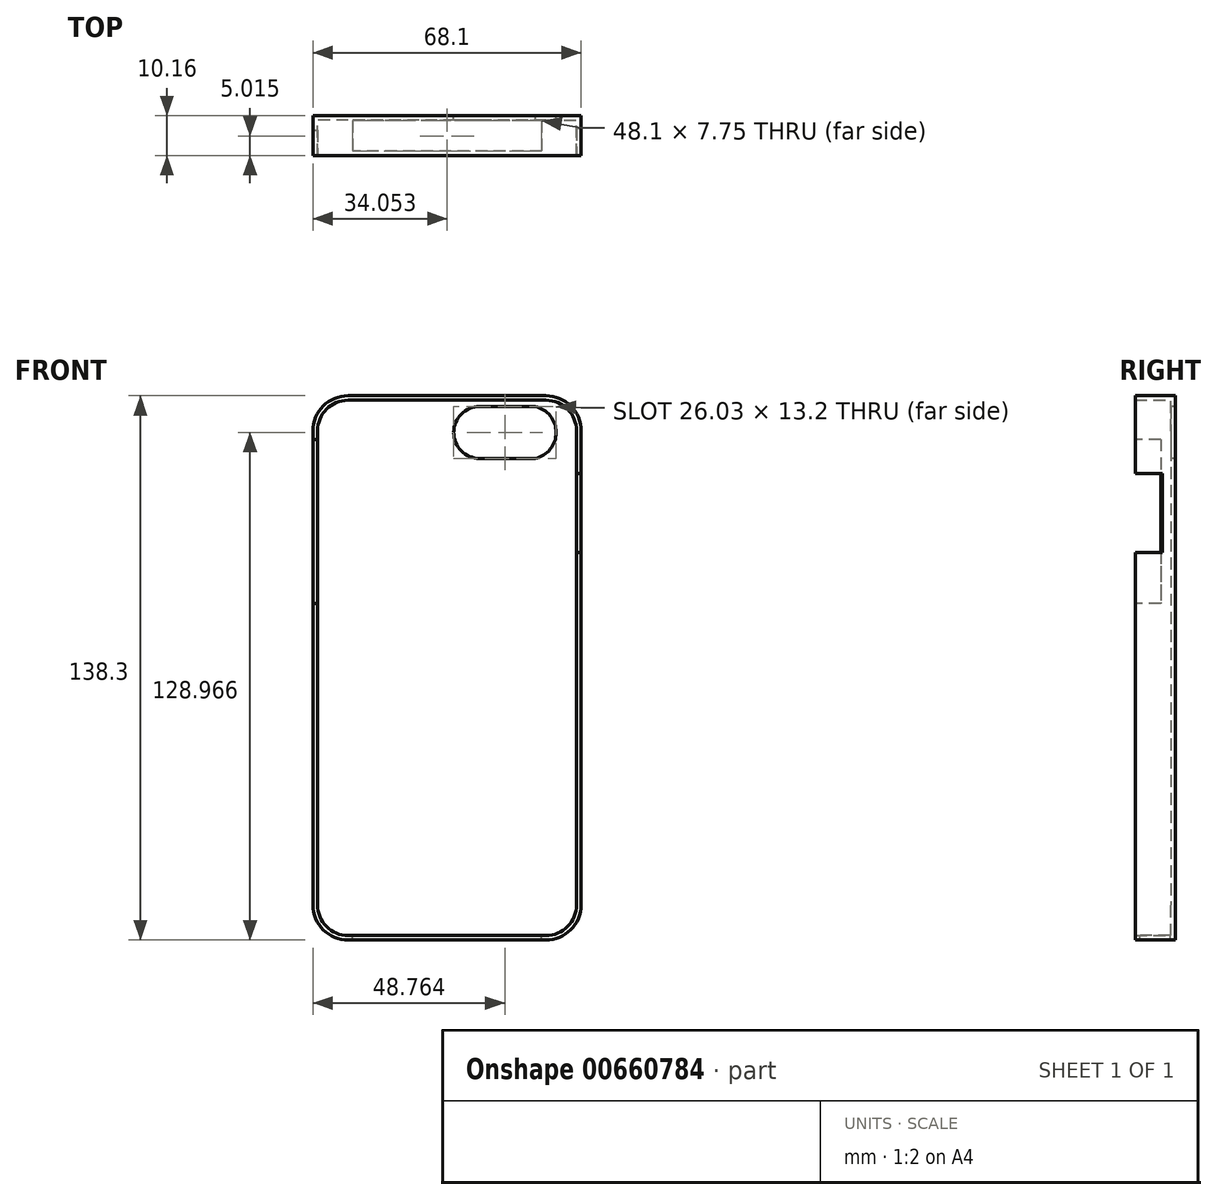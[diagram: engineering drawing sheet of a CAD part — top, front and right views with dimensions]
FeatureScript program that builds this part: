
annotation { "Feature Type Name" : "Feature", "Feature Type Description" : "" }
export const myFeature = defineFeature(function(context is Context, id is Id, definition is map)
    precondition{}
    {
        {
            var Q0;
            Q0=qCreatedBy(makeId("Front.planeOp"),FACE);
            var sketch = newSketch(context, id + "F0", { "sketchPlane" : qUnion([Q0])});
            skLineSegment(sketch, "E0.bottom", {"start": v(34.05, 69.15) * mm, "end": v(-34.05, 69.15) * mm});
            skLineSegment(sketch, "E0.top", {"start": v(34.05, -69.15) * mm, "end": v(-34.05, -69.15) * mm});
            skLineSegment(sketch, "E0.left", {"start": v(34.05, 69.15) * mm, "end": v(34.05, -69.15) * mm});
            skLineSegment(sketch, "E0.right", {"start": v(-34.05, 69.15) * mm, "end": v(-34.05, -69.15) * mm});
            skPoint(sketch, "E0.middle", {"position": v(0, 0) * mm});
            skSolve(sketch);
        }
        {
            var Q0;
            Q0=makeQuery(id+"F0.imprint","IMPRINT",FACE,{"disambiguationData":[TD([[makeQuery(id+"F0.imprint","IMPRINT",EDGE,{"derivedFrom":sQuery(id+"F0.wireOp",EDGE,"E0.bottom")}),1.0]])]});
            extrude(context, id + "F1", {"entities" : qUnion([Q0]), "endBound" : BoundingType.SYMMETRIC, "depth" : 10.16 * mm});
        }
        {
            var Q0;
            Q0=makeQuery(id+"F1.opExtrude","SWEPT_EDGE",EDGE,{"disambiguationData":[OSD([sQuery(id+"F0.wireOp",EDGE,"E0.bottom"),sQuery(id+"F0.wireOp",EDGE,"E0.right")])]});
            var Q1;
            Q1=makeQuery(id+"F1.opExtrude","SWEPT_EDGE",EDGE,{"disambiguationData":[OSD([sQuery(id+"F0.wireOp",EDGE,"E0.bottom"),sQuery(id+"F0.wireOp",EDGE,"E0.left")])]});
            var Q2;
            Q2=makeQuery(id+"F1.opExtrude","SWEPT_EDGE",EDGE,{"disambiguationData":[OSD([sQuery(id+"F0.wireOp",EDGE,"E0.top"),sQuery(id+"F0.wireOp",EDGE,"E0.left")])]});
            var Q3;
            Q3=makeQuery(id+"F1.opExtrude","SWEPT_EDGE",EDGE,{"disambiguationData":[OSD([sQuery(id+"F0.wireOp",EDGE,"E0.top"),sQuery(id+"F0.wireOp",EDGE,"E0.right")])]});
            fillet(context, id + "F2", {"entities" : qUnion([Q0, Q1, Q2, Q3]), "radius" : 8.93 * mm, "tangentPropagation" : true, "allowEdgeOverflow" : false});
        }
        {
            var Q0;
            Q0=makeQuery(id+"F1.opExtrude","CAP_FACE",FACE,{"disambiguationData":[OSD([sQuery(id+"F0.wireOp",EDGE,"E0.bottom"),sQuery(id+"F0.wireOp",EDGE,"E0.top"),sQuery(id+"F0.wireOp",EDGE,"E0.left"),sQuery(id+"F0.wireOp",EDGE,"E0.right")])],"isStart":false});
            shell(context, id + "F3", {"entities" : qUnion([Q0]), "thickness" : 1.15 * mm});
        }
        {
            var Q0;
            Q0=makeQuery(id+"F0.imprint","IMPRINT",FACE,{"disambiguationData":[TD([[makeQuery(id+"F0.imprint","IMPRINT",EDGE,{"derivedFrom":sQuery(id+"F0.wireOp",EDGE,"E0.bottom")}),1.0]])]});
            var sketch = newSketch(context, id + "F4", { "sketchPlane" : qUnion([Q0])});
            skLineSegment(sketch, "E1.bottom", {"start": v(27.4, 66.41) * mm, "end": v(3.3, 66.41) * mm});
            skLineSegment(sketch, "E1.top", {"start": v(27.4, 53.22) * mm, "end": v(3.3, 53.22) * mm});
            skLineSegment(sketch, "E1.left", {"start": v(27.4, 66.41) * mm, "end": v(27.4, 53.22) * mm});
            skLineSegment(sketch, "E1.right", {"start": v(3.3, 66.41) * mm, "end": v(3.3, 53.22) * mm});
            skSolve(sketch);
        }
        {
            var Q0;
            Q0=qSketchRegion(id+"F4",true);
            extrude(context, id + "F5", {"entities" : qUnion([Q0]), "operationType" : NewBodyOperationType.REMOVE, "endBound" : BoundingType.SYMMETRIC, "depth" : 25 * mm});
        }
        {
            var Q0;
            Q0=makeQuery(id+"F1.opExtrude","SWEPT_FACE",FACE,{"disambiguationData":[OSD([sQuery(id+"F0.wireOp",EDGE,"E0.top")])]});
            var sketch = newSketch(context, id + "F6", { "sketchPlane" : qUnion([Q0])});
            skLineSegment(sketch, "E2.bottom", {"start": v(-24.05, 3.94) * mm, "end": v(24.05, 3.94) * mm});
            skLineSegment(sketch, "E2.top", {"start": v(-24.05, -3.81) * mm, "end": v(24.05, -3.81) * mm});
            skLineSegment(sketch, "E2.left", {"start": v(-24.05, 3.94) * mm, "end": v(-24.05, -3.81) * mm});
            skLineSegment(sketch, "E2.right", {"start": v(24.05, 3.94) * mm, "end": v(24.05, -3.81) * mm});
            skSolve(sketch);
        }
        {
            var Q0;
            {var subQ0=sQuery(id+"F6.wireOp",EDGE,"E2.bottom");Q0=makeQuery(id+"F6.imprint","IMPRINT",FACE,{"disambiguationData":[TD([[makeQuery(id+"F6.imprint","IMPRINT",EDGE,{"derivedFrom":subQ0}),-1.0]])]});}
            var Q1;
            {var subQ0=sQuery(id+"F6.wireOp",EDGE,"E2.top");Q1=makeQuery(id+"F6.imprint","IMPRINT",FACE,{"disambiguationData":[TD([[makeQuery(id+"F6.imprint","IMPRINT",EDGE,{"derivedFrom":subQ0}),1.0]])]});}
            extrude(context, id + "F7", {"entities" : qUnion([Q0, Q1]), "operationType" : NewBodyOperationType.REMOVE, "endBound" : BoundingType.SYMMETRIC, "depth" : 25 * mm});
        }
        {
            var Q0;
            Q0=makeQuery(id+"F1.opExtrude","SWEPT_FACE",FACE,{"disambiguationData":[OSD([sQuery(id+"F0.wireOp",EDGE,"E0.right")])]});
            var sketch = newSketch(context, id + "F8", { "sketchPlane" : qUnion([Q0])});
            skLineSegment(sketch, "E3.bottom", {"start": v(-1.38, 58.06) * mm, "end": v(8.73, 58.06) * mm});
            skLineSegment(sketch, "E3.top", {"start": v(-1.38, 16.4) * mm, "end": v(8.73, 16.4) * mm});
            skLineSegment(sketch, "E3.left", {"start": v(-1.38, 58.06) * mm, "end": v(-1.38, 16.4) * mm});
            skLineSegment(sketch, "E3.right", {"start": v(8.73, 58.06) * mm, "end": v(8.73, 16.4) * mm});
            skSolve(sketch);
        }
        {
            var Q0;
            Q0=qSketchRegion(id+"F8",true);
            extrude(context, id + "F9", {"entities" : qUnion([Q0]), "operationType" : NewBodyOperationType.REMOVE, "endBound" : BoundingType.SYMMETRIC, "depth" : 25 * mm});
        }
        {
            var Q0;
            Q0=makeQuery(id+"F1.opExtrude","SWEPT_FACE",FACE,{"disambiguationData":[OSD([sQuery(id+"F0.wireOp",EDGE,"E0.left")])]});
            var sketch = newSketch(context, id + "F10", { "sketchPlane" : qUnion([Q0])});
            skLineSegment(sketch, "E4.bottom", {"start": v(-5.08, 49.35) * mm, "end": v(1.78, 49.35) * mm});
            skLineSegment(sketch, "E4.top", {"start": v(-5.08, 29.37) * mm, "end": v(1.78, 29.37) * mm});
            skLineSegment(sketch, "E4.left", {"start": v(-5.08, 49.35) * mm, "end": v(-5.08, 29.37) * mm});
            skLineSegment(sketch, "E4.right", {"start": v(1.78, 49.35) * mm, "end": v(1.78, 29.37) * mm});
            skSolve(sketch);
        }
        {
            var Q0;
            Q0=makeQuery(id+"F10.imprint","IMPRINT",FACE,{"disambiguationData":[TD([[makeQuery(id+"F10.imprint","IMPRINT",EDGE,{"derivedFrom":sQuery(id+"F10.wireOp",EDGE,"E4.bottom")}),-1.0]])]});
            extrude(context, id + "F11", {"entities" : qUnion([Q0]), "operationType" : NewBodyOperationType.REMOVE, "endBound" : BoundingType.SYMMETRIC, "depth" : 25 * mm});
        }
        {
            var Q0;
            Q0=makeQuery(id+"F5.boolean.opBoolean","COPY",EDGE,{"derivedFrom":makeQuery(id+"F5.opExtrude","SWEPT_EDGE",EDGE,{"disambiguationData":[OSD([sQuery(id+"F4.wireOp",EDGE,"E1.bottom"),sQuery(id+"F4.wireOp",EDGE,"E1.right")])]})});
            var Q1;
            Q1=makeQuery(id+"F5.boolean.opBoolean","COPY",EDGE,{"derivedFrom":makeQuery(id+"F5.opExtrude","SWEPT_EDGE",EDGE,{"disambiguationData":[OSD([sQuery(id+"F4.wireOp",EDGE,"E1.bottom"),sQuery(id+"F4.wireOp",EDGE,"E1.left")])]})});
            var Q2;
            Q2=makeQuery(id+"F5.boolean.opBoolean","COPY",EDGE,{"derivedFrom":makeQuery(id+"F5.opExtrude","SWEPT_EDGE",EDGE,{"disambiguationData":[OSD([sQuery(id+"F4.wireOp",EDGE,"E1.top"),sQuery(id+"F4.wireOp",EDGE,"E1.left")])]})});
            var Q3;
            Q3=makeQuery(id+"F5.boolean.opBoolean","COPY",EDGE,{"derivedFrom":makeQuery(id+"F5.opExtrude","SWEPT_EDGE",EDGE,{"disambiguationData":[OSD([sQuery(id+"F4.wireOp",EDGE,"E1.top"),sQuery(id+"F4.wireOp",EDGE,"E1.right")])]})});
            chamfer(context, id + "F12", {"entities" : qUnion([Q0, Q1, Q2, Q3]), "width" : 5 * mm, "tangentPropagation" : true});
        }
        {
            var Q0;
            Q0=makeQuery(id+"F1.opExtrude","CAP_FACE",FACE,{"disambiguationData":[OSD([sQuery(id+"F0.wireOp",EDGE,"E0.bottom"),sQuery(id+"F0.wireOp",EDGE,"E0.top"),sQuery(id+"F0.wireOp",EDGE,"E0.left"),sQuery(id+"F0.wireOp",EDGE,"E0.right")])],"isStart":true});
            var sketch = newSketch(context, id + "F13", { "sketchPlane" : qUnion([Q0])});
            skArc(sketch, "E5", {"start": v(-22.4, 66.41) * mm, "mid": v(-27.73, 59.82) * mm, "end": v(-22.4, 53.22) * mm});
            skArc(sketch, "E6", {"start": v(-8.3, 53.22) * mm, "mid": v(-3.22, 59.82) * mm, "end": v(-8.3, 66.41) * mm});
            skSolve(sketch);
        }
        {
            var Q0;
            Q0 = qSketchRegion(id + "F13", true);
            var Q1;
            Q1=makeQuery(id+"F13.imprint","IMPRINT",FACE,{"disambiguationData":[TD([[makeQuery(id+"F13.imprint","IMPRINT",EDGE,{"derivedFrom":sQuery(id+"F13.wireOp",EDGE,"E5")}),1.0]])]});
            extrude(context, id + "F14", {"entities" : qUnion([Q0, Q1]), "operationType" : NewBodyOperationType.REMOVE, "oppositeDirection" : true, "depth" : 25 * mm, "offsetDistance" : 25 * mm});
        }
        {
            var Q0;
            Q0=makeQuery(id+"F1.opExtrude","CAP_FACE",FACE,{"disambiguationData":[OSD([sQuery(id+"F0.wireOp",EDGE,"E0.bottom"),sQuery(id+"F0.wireOp",EDGE,"E0.top"),sQuery(id+"F0.wireOp",EDGE,"E0.left"),sQuery(id+"F0.wireOp",EDGE,"E0.right")])],"isStart":true});
            var sketch = newSketch(context, id + "F15", { "sketchPlane" : qUnion([Q0])});
            skArc(sketch, "E7", {"start": v(-8.3, 53.22) * mm, "mid": v(-1.7, 59.82) * mm, "end": v(-8.3, 66.41) * mm});
            skSolve(sketch);
        }
        {
            var Q0;
            Q0 = qSketchRegion(id + "F15", true);
            var Q1;
            Q1=makeQuery(id+"F15.imprint","IMPRINT",FACE,{"disambiguationData":[TD([[makeQuery(id+"F15.imprint","IMPRINT",EDGE,{"derivedFrom":sQuery(id+"F15.wireOp",EDGE,"E7")}),1.0]])]});
            extrude(context, id + "F16", {"entities" : qUnion([Q0, Q1]), "operationType" : NewBodyOperationType.REMOVE, "oppositeDirection" : true, "depth" : 25 * mm, "offsetDistance" : 25 * mm});
        }
    });
